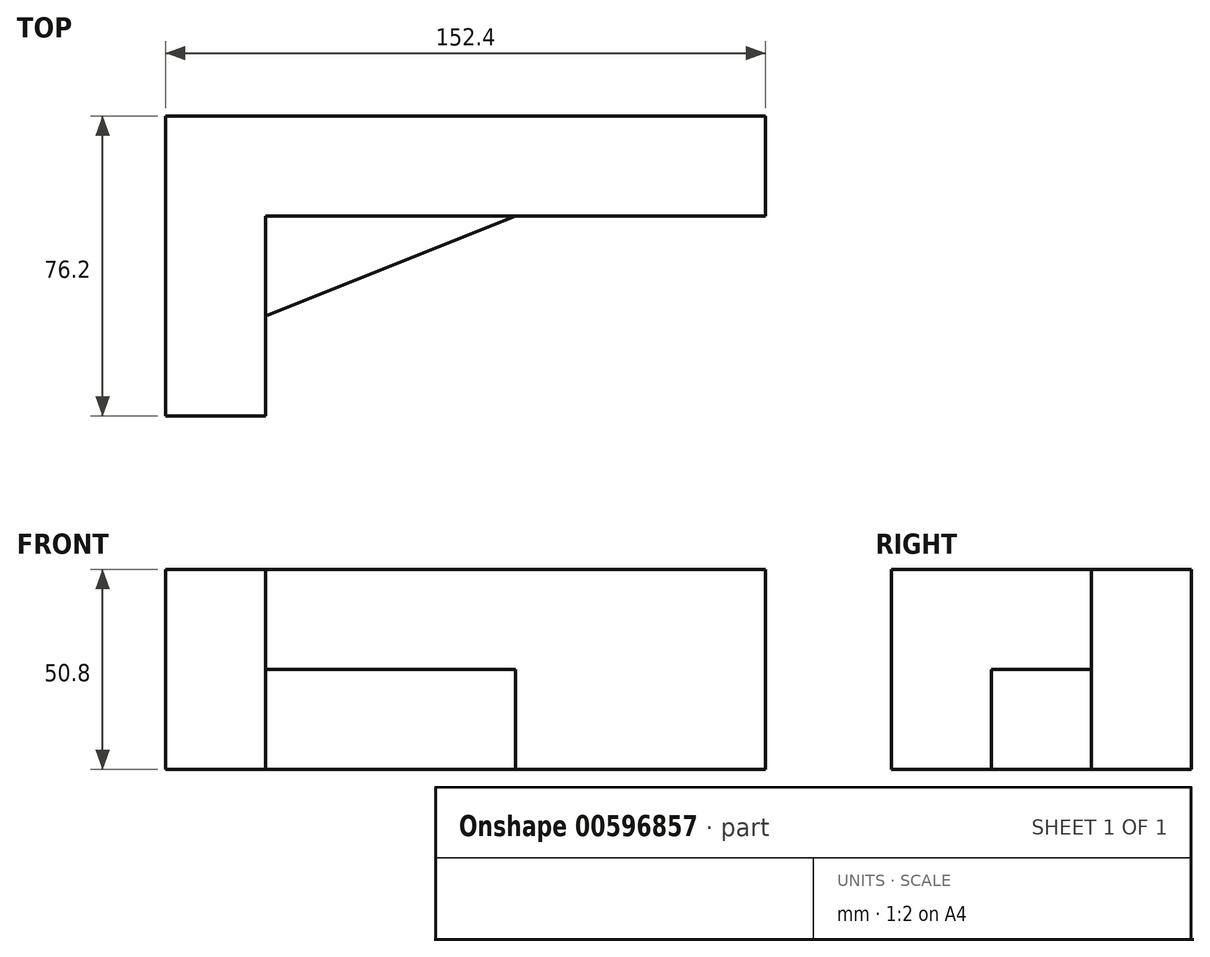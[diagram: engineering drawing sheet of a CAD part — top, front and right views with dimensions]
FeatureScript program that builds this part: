
annotation { "Feature Type Name" : "Feature", "Feature Type Description" : "" }
export const myFeature = defineFeature(function(context is Context, id is Id, definition is map)
    precondition{}
    {
        {
            var Q0;
            Q0=qCreatedBy(makeId("Top.planeOp"),FACE);
            var sketch = newSketch(context, id + "F0", { "sketchPlane" : qUnion([Q0])});
            skLineSegment(sketch, "E0", {"start": v(0, 0) * mm, "end": v(0, 76.2) * mm});
            skLineSegment(sketch, "E1", {"start": v(0, 76.2) * mm, "end": v(152.4, 76.2) * mm});
            skLineSegment(sketch, "E2", {"start": v(152.4, 76.2) * mm, "end": v(152.4, 50.8) * mm});
            skLineSegment(sketch, "E3", {"start": v(152.4, 50.8) * mm, "end": v(25.4, 50.8) * mm});
            skLineSegment(sketch, "E4", {"start": v(25.4, 50.8) * mm, "end": v(25.4, 0) * mm});
            skLineSegment(sketch, "E5", {"start": v(25.4, 0) * mm, "end": v(0, 0) * mm});
            skSolve(sketch);
        }
        {
            var Q0;
            Q0=makeQuery(id+"F0.imprint","IMPRINT",FACE,{"disambiguationData":[TD([[makeQuery(id+"F0.imprint","IMPRINT",EDGE,{"derivedFrom":sQuery(id+"F0.wireOp",EDGE,"E0")}),-1.0]])]});
            extrude(context, id + "F1", {"entities" : qUnion([Q0]), "depth" : 50.8 * mm, "offsetDistance" : 25.4 * mm});
        }
        {
            var Q0;
            Q0=makeQuery(id+"F1.opExtrude","CAP_FACE",FACE,{"disambiguationData":[OSD([sQuery(id+"F0.wireOp",EDGE,"E0"),sQuery(id+"F0.wireOp",EDGE,"E1"),sQuery(id+"F0.wireOp",EDGE,"E2"),sQuery(id+"F0.wireOp",EDGE,"E3"),sQuery(id+"F0.wireOp",EDGE,"E4"),sQuery(id+"F0.wireOp",EDGE,"E5")])],"isStart":false});
            var sketch = newSketch(context, id + "F2", { "sketchPlane" : qUnion([Q0])});
            skLineSegment(sketch, "E6", {"start": v(25.4, 25.4) * mm, "end": v(88.9, 50.8) * mm});
            skSolve(sketch);
        }
        {
            var Q0;
            {var subQ0=sQuery(id+"F2.wireOp",EDGE,"E6");Q0=makeQuery(id+"F2.imprint","IMPRINT",FACE,{"disambiguationData":[TD([[makeQuery(id+"F2.imprint","IMPRINT",EDGE,{"derivedFrom":subQ0}),1.0]])]});}
            extrude(context, id + "F3", {"entities" : qUnion([Q0]), "operationType" : NewBodyOperationType.ADD, "oppositeDirection" : true, "depth" : 50.8 * mm, "offsetDistance" : 25.4 * mm});
        }
        {
            var Q0;
            {var subQ0=sQuery(id+"F0.wireOp",EDGE,"E4");var subQ1=sQuery(id+"F0.wireOp",EDGE,"E3");Q0=makeQuery(id+"F3.boolean.opBoolean","MERGE",FACE,{"derivedFrom":[makeQuery(id+"F1.opExtrude","CAP_FACE",FACE,{"disambiguationData":[OSD([sQuery(id+"F0.wireOp",EDGE,"E0"),sQuery(id+"F0.wireOp",EDGE,"E1"),sQuery(id+"F0.wireOp",EDGE,"E2"),subQ1,subQ0,sQuery(id+"F0.wireOp",EDGE,"E5")])],"isStart":false}),makeQuery(id+"F3.opExtrude","CAP_FACE",FACE,{"disambiguationData":[OSD([subQ1,subQ0,sQuery(id+"F2.wireOp",EDGE,"E6")])],"isStart":true})]});}
            var sketch = newSketch(context, id + "F4", { "sketchPlane" : qUnion([Q0])});
            skLineSegment(sketch, "E7", {"start": v(88.9, 50.8) * mm, "end": v(25.4, 50.8) * mm});
            skLineSegment(sketch, "E8", {"start": v(25.4, 50.8) * mm, "end": v(25.4, 25.4) * mm});
            skSolve(sketch);
        }
        {
            var Q0;
            Q0=makeQuery(id+"F4.imprint","IMPRINT",FACE,{"disambiguationData":[TD([[makeQuery(id+"F4.imprint","IMPRINT",EDGE,{"derivedFrom":sQuery(id+"F4.wireOp",EDGE,"E7")}),1.0]])]});
            extrude(context, id + "F5", {"entities" : qUnion([Q0]), "operationType" : NewBodyOperationType.REMOVE, "oppositeDirection" : true, "depth" : 25.4 * mm, "offsetDistance" : 25.4 * mm});
        }
    });
